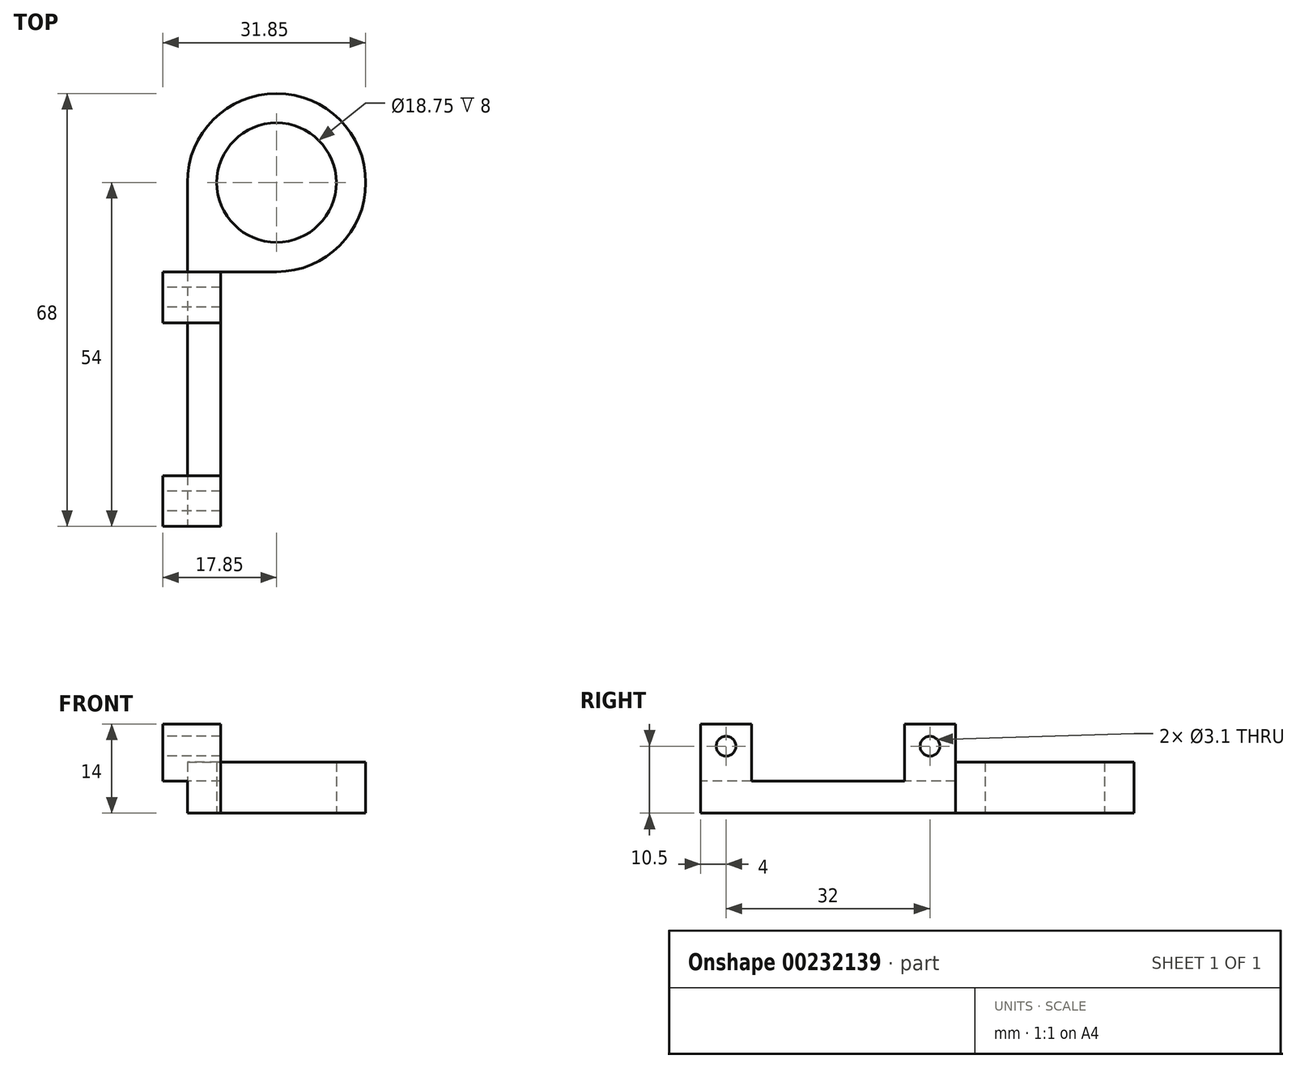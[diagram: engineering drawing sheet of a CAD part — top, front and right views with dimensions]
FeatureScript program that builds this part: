
annotation { "Feature Type Name" : "Feature", "Feature Type Description" : "" }
export const myFeature = defineFeature(function(context is Context, id is Id, definition is map)
    precondition{}
    {
        {
            var Q0;
            Q0=qCreatedBy(makeId("Top.planeOp"),FACE);
            var sketch = newSketch(context, id + "F0", { "sketchPlane" : qUnion([Q0])});
            skArc(sketch, "E0", {"start": v(0, 0) * mm, "mid": v(9.9, 23.9) * mm, "end": v(-14, 14) * mm});
            skLineSegment(sketch, "E1", {"start": v(-14, 14) * mm, "end": v(-14, 0) * mm});
            skPoint(sketch, "E2.right.end.orphan", {"position": v(0, 5.25) * mm});
            skPoint(sketch, "E3.0", {"position": v(0, 0) * mm});
            skLineSegment(sketch, "E4", {"start": v(0, 0) * mm, "end": v(0, 28) * mm, "construction": true});
            skCircle(sketch, "E5", {"center": v(0, 14) * mm, "radius": 9.38 * mm});
            skLineSegment(sketch, "E6", {"start": v(-14, 0) * mm, "end": v(0, 0) * mm});
            skSolve(sketch);
        }
        {
            var Q0;
            Q0 = qSketchRegion(id + "F0", true);
            extrude(context, id + "F1", {"entities" : qUnion([Q0]), "depth" : 8 * mm});
        }
        {
            var Q0;
            Q0=qCreatedBy(makeId("Top.planeOp"),FACE);
            var sketch = newSketch(context, id + "F2", { "sketchPlane" : qUnion([Q0])});
            skLineSegment(sketch, "E7.0.0", {"start": v(-14, 0) * mm, "end": v(0, 0) * mm});
            skLineSegment(sketch, "E7.0.2", {"start": v(0, 0) * mm, "end": v(-14, 0) * mm});
            skLineSegment(sketch, "E8.bottom", {"start": v(-14, 0) * mm, "end": v(-8.75, 0) * mm});
            skLineSegment(sketch, "E8.top", {"start": v(-14, -40) * mm, "end": v(-8.75, -40) * mm});
            skLineSegment(sketch, "E8.right", {"start": v(-8.75, 0) * mm, "end": v(-8.75, -40) * mm});
            skLineSegment(sketch, "E9", {"start": v(-14, 0) * mm, "end": v(-14, -40) * mm});
            skSolve(sketch);
        }
        {
            var Q0;
            Q0 = qSketchRegion(id + "F2", true);
            extrude(context, id + "F3", {"entities" : qUnion([Q0]), "operationType" : NewBodyOperationType.ADD, "depth" : 5 * mm});
        }
        {
            var Q0;
            Q0=makeQuery(id+"F3.opExtrude","CAP_FACE",FACE,{"disambiguationData":[OSD([sQuery(id+"F2.wireOp",EDGE,"E8.bottom"),sQuery(id+"F2.wireOp",EDGE,"E8.top"),sQuery(id+"F2.wireOp",EDGE,"E8.right"),sQuery(id+"F2.wireOp",EDGE,"E9")])],"isStart":false});
            var sketch = newSketch(context, id + "F4", { "sketchPlane" : qUnion([Q0])});
            skLineSegment(sketch, "E10.0", {"start": v(-14, 0) * mm, "end": v(-8.75, 0) * mm});
            skLineSegment(sketch, "E11.0", {"start": v(-14, -40) * mm, "end": v(-8.75, -40) * mm});
            skLineSegment(sketch, "E12.0", {"start": v(-8.75, 0) * mm, "end": v(-8.75, -40) * mm});
            skLineSegment(sketch, "E13.bottom", {"start": v(-8.75, 0) * mm, "end": v(-17.85, 0) * mm});
            skLineSegment(sketch, "E13.top", {"start": v(-8.75, -8) * mm, "end": v(-17.85, -8) * mm});
            skLineSegment(sketch, "E13.left", {"start": v(-8.75, 0) * mm, "end": v(-8.75, -8) * mm});
            skLineSegment(sketch, "E13.right", {"start": v(-17.85, 0) * mm, "end": v(-17.85, -8) * mm});
            skLineSegment(sketch, "E14.bottom", {"start": v(-8.75, -40) * mm, "end": v(-17.85, -40) * mm});
            skLineSegment(sketch, "E14.top", {"start": v(-8.75, -32) * mm, "end": v(-17.85, -32) * mm});
            skLineSegment(sketch, "E14.left", {"start": v(-8.75, -40) * mm, "end": v(-8.75, -32) * mm});
            skLineSegment(sketch, "E14.right", {"start": v(-17.85, -40) * mm, "end": v(-17.85, -32) * mm});
            skSolve(sketch);
        }
        {
            var Q0;
            Q0 = qSketchRegion(id + "F4", true);
            extrude(context, id + "F5", {"entities" : qUnion([Q0]), "operationType" : NewBodyOperationType.ADD, "depth" : 9 * mm});
        }
        {
            var Q0;
            Q0=makeQuery(id+"F5.opExtrude","SWEPT_FACE",FACE,{"disambiguationData":[OSD([sQuery(id+"F4.wireOp",EDGE,"E13.right")])]});
            var sketch = newSketch(context, id + "F6", { "sketchPlane" : qUnion([Q0])});
            skLineSegment(sketch, "E15.0", {"start": v(0, 14) * mm, "end": v(0, 5) * mm});
            skLineSegment(sketch, "E16.0", {"start": v(0, 14) * mm, "end": v(8, 14) * mm});
            skLineSegment(sketch, "E17.0", {"start": v(32, 14) * mm, "end": v(32, 5) * mm});
            skLineSegment(sketch, "E18.0", {"start": v(40, 14) * mm, "end": v(32, 14) * mm});
            skPoint(sketch, "E19", {"position": v(4, 10.5) * mm});
            skPoint(sketch, "E20", {"position": v(36, 10.5) * mm});
            skSolve(sketch);
        }
        {
            var Q0;
            Q0=sQuery(id+"F6.wireOp",VERTEX,"E19");
            var Q1;
            Q1=sQuery(id+"F6.wireOp",VERTEX,"E20");
            var Q2;
            Q2=makeQuery(id+"F1.opExtrude","SWEPT_BODY",BODY,{"disambiguationData":[OSD([sQuery(id+"F0.wireOp",EDGE,"E0"),sQuery(id+"F0.wireOp",EDGE,"E1"),sQuery(id+"F0.wireOp",EDGE,"E5"),sQuery(id+"F0.wireOp",EDGE,"E6")])]});
            hole(context, id + "F7", {"style" : HoleStyle.SIMPLE, "endStyle" : HoleEndStyle.THROUGH, "holeDiameter" : 3.1 * mm, "startFromSketch" : true, "locations" : qUnion([Q0, Q1]), "scope" : qUnion([Q2]), "isTappedThrough" : true});
        }
    });
